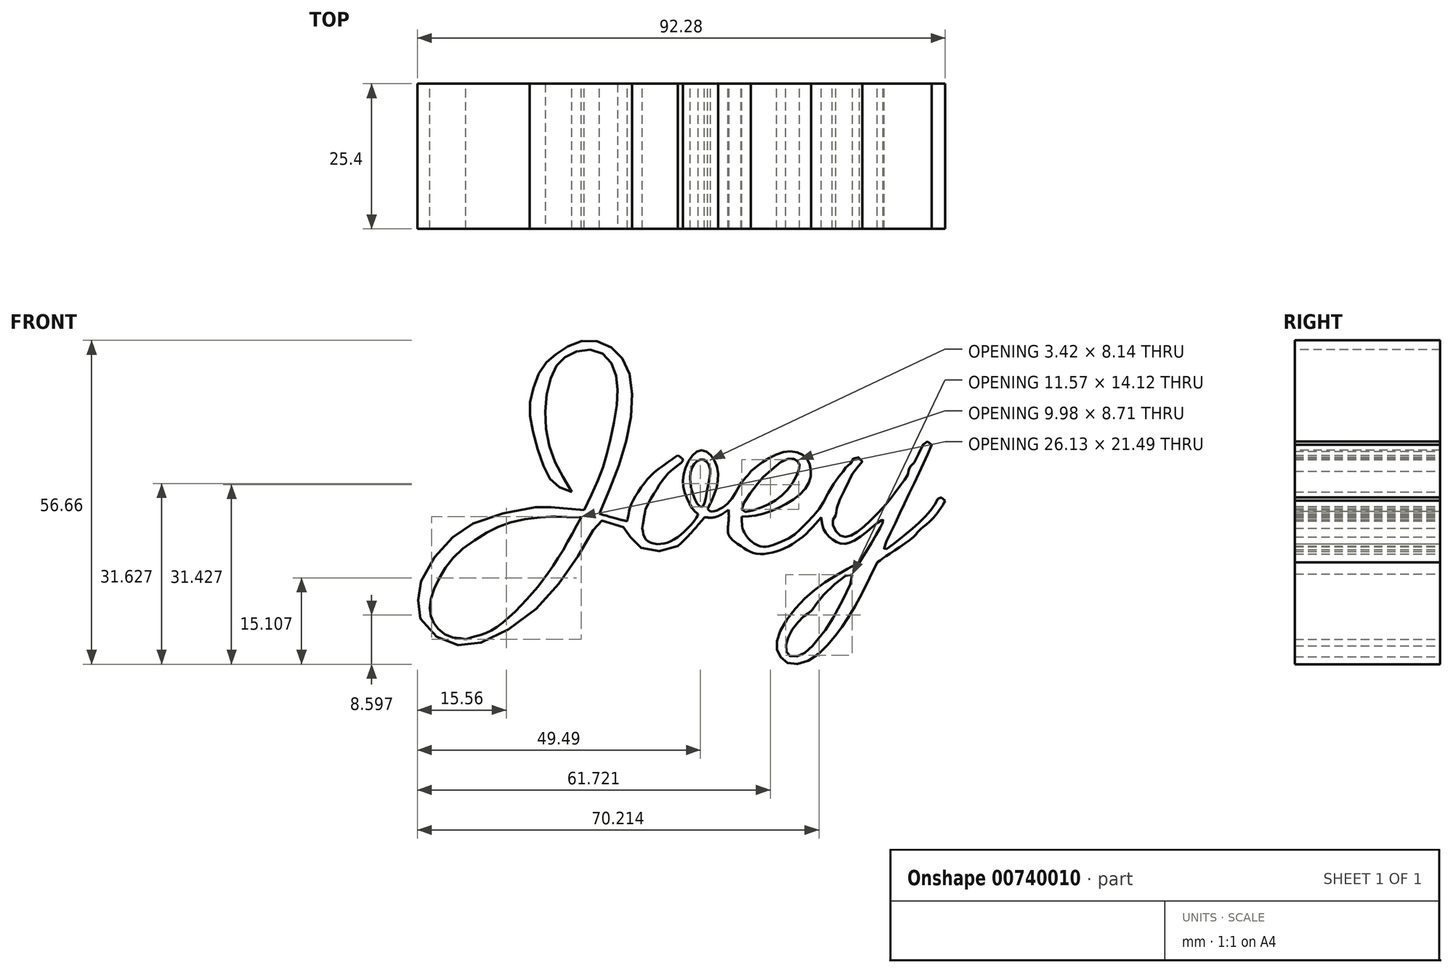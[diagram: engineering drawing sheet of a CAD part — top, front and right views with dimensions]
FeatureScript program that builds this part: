
annotation { "Feature Type Name" : "Feature", "Feature Type Description" : "" }
export const myFeature = defineFeature(function(context is Context, id is Id, definition is map)
    precondition{}
    {
        {
            var Q0;
            Q0=qCreatedBy(makeId("Front.planeOp"),FACE);
            var sketch = newSketch(context, id + "F0", { "sketchPlane" : qUnion([Q0])});
            skFitSpline(sketch, "E0", {"points": [v(-17.96, 22.58) * mm, v(-15.07, 28.97) * mm, v(-13.67, 33.7) * mm, v(-12.17, 41.56) * mm, v(-12.6, 47.01) * mm, v(-15.4, 50.4) * mm, v(-20.27, 49.96) * mm, v(-23.07, 47.3) * mm, v(-24.69, 40.68) * mm, v(-23.66, 32.72) * mm, v(-20.12, 25.8) * mm], "startDerivative": vector(30.1, 62.52) * mm, "endDerivative": vector(35.55, -58.87) * mm});
            skFitSpline(sketch, "E1", {"points": [v(-20.12, 25.8) * mm, v(-23.36, 27.42) * mm, v(-25.57, 31.84) * mm, v(-27.34, 38.61) * mm, v(-27.2, 42.6) * mm, v(-25.28, 47.45) * mm, v(-22.77, 49.96) * mm, v(-18.5, 52.17) * mm, v(-13.5, 51.28) * mm, v(-10.1, 46.72) * mm, v(-10.25, 35.96) * mm, v(-15.26, 21.97) * mm], "startDerivative": vector(-50.27, 16.62) * mm, "endDerivative": vector(-41.8, -97.9) * mm});
            skFitSpline(sketch, "E2", {"points": [v(-15.26, 21.97) * mm, v(-11.6, 20.94) * mm, v(-10.4, 20.67) * mm], "startDerivative": vector(6.52, -1.9) * mm, "endDerivative": vector(2.88, -0.56) * mm});
            skFitSpline(sketch, "E3", {"points": [v(-10.4, 20.67) * mm, v(-10.07, 22.34) * mm, v(-9.83, 23.37) * mm, v(-7.01, 27.85) * mm, v(-4.2, 30.34) * mm, v(-1.58, 32.18) * mm], "startDerivative": vector(2.54, 11.82) * mm, "endDerivative": vector(12.38, 8.58) * mm});
            skFitSpline(sketch, "E4", {"points": [v(-1.58, 32.18) * mm, v(-0.66, 31.3) * mm, v(-2.41, 29.77) * mm, v(-5, 26.66) * mm, v(-7.1, 22.98) * mm, v(-7.36, 21.97) * mm, v(-7.76, 19.44) * mm], "startDerivative": vector(11.74, -6.98) * mm, "endDerivative": vector(-2.67, -16.96) * mm});
            skFitSpline(sketch, "E5", {"points": [v(-17.96, 22.58) * mm, v(-24.78, 23.2) * mm, v(-25.98, 23.2) * mm, v(-33.9, 21.58) * mm, v(-39.38, 19.06) * mm, v(-42.92, 15.84) * mm, v(-46.3, 10.63) * mm, v(-46.88, 7.45) * mm, v(-47.07, 5.45) * mm, v(-45.4, 1.85) * mm, v(-41.55, -0.63) * mm, v(-38.02, -1.06) * mm, v(-32.57, 0.92) * mm, v(-25.2, 6.37) * mm, v(-20, 13.13) * mm, v(-16.25, 19.38) * mm, v(-15.66, 20.85) * mm, v(-12.16, 19.82) * mm, v(-10.4, 19.36) * mm, v(-9.83, 17.94) * mm, v(-8.98, 16.83) * mm, v(-7.1, 15.56) * mm, v(-4.18, 15.53) * mm, v(-1.58, 16.3) * mm], "startDerivative": vector(-148.87, 13.53) * mm, "endDerivative": vector(69.66, 24.55) * mm});
            skFitSpline(sketch, "E6", {"points": [v(-18.46, 21.37) * mm, v(-23.55, 12.53) * mm, v(-29, 5.9) * mm, v(-34.38, 1.4) * mm, v(-37.24, 0.48) * mm, v(-38.64, 0) * mm], "startDerivative": vector(-18, -33.91) * mm, "endDerivative": vector(-12.44, -4.8) * mm});
            skFitSpline(sketch, "E7", {"points": [v(-38.64, 0) * mm, v(-39.6, 0.17) * mm, v(-41.55, 0.52) * mm, v(-43.46, 1.84) * mm, v(-44.34, 3.15) * mm, v(-44.9, 4.99) * mm, v(-44.6, 7.49) * mm, v(-42.93, 11.3) * mm, v(-39.9, 15.18) * mm, v(-34.6, 18.84) * mm, v(-29.64, 20.76) * mm, v(-23.73, 21.49) * mm, v(-23, 21.49) * mm, v(-18.46, 21.37) * mm], "startDerivative": vector(-20.04, 4.15) * mm, "endDerivative": vector(60.78, -1.5) * mm});
            skFitSpline(sketch, "E8", {"points": [v(-7.76, 19.44) * mm, v(-7.04, 17.4) * mm, v(-4.75, 16.66) * mm, v(-1.83, 17.7) * mm, v(1.34, 20.78) * mm, v(2.02, 21.92) * mm], "startDerivative": vector(1.9, -12.67) * mm, "endDerivative": vector(3.32, 6.96) * mm});
            skFitSpline(sketch, "E9", {"points": [v(2.02, 21.92) * mm, v(1.03, 22.84) * mm, v(0, 24.79) * mm, v(-0.66, 27.42) * mm, v(0, 30.41) * mm, v(1.86, 32.91) * mm, v(3.64, 32.7) * mm, v(5.25, 30.26) * mm, v(5.3, 26.87) * mm, v(3.69, 22.84) * mm], "startDerivative": vector(-13.04, 10.03) * mm, "endDerivative": vector(-13.9, -28.86) * mm});
            skFitSpline(sketch, "E10", {"points": [v(3.69, 22.84) * mm, v(4.2, 22.4) * mm, v(5.88, 22.84) * mm, v(7.9, 24.63) * mm, v(9.31, 27.03) * mm, v(10.1, 28.03) * mm, v(11.24, 29.42) * mm], "startDerivative": vector(3.95, -5.47) * mm, "endDerivative": vector(7.15, 8.9) * mm});
            skFitSpline(sketch, "E11", {"points": [v(2.75, 23.2) * mm, v(3.69, 26.66) * mm, v(4.1, 29.84) * mm, v(3.17, 31.3) * mm, v(2.02, 31.3) * mm, v(0.82, 29.79) * mm, v(0.77, 26.56) * mm, v(1.86, 23.75) * mm, v(2.75, 23.2) * mm]});
            skFitSpline(sketch, "E12", {"points": [v(-1.58, 16.3) * mm, v(0.46, 18.29) * mm, v(3.12, 21.37) * mm], "startDerivative": vector(4.38, 4.07) * mm, "endDerivative": vector(4.99, 6) * mm});
            skFitSpline(sketch, "E13", {"points": [v(3.12, 21.37) * mm, v(4.94, 21.37) * mm, v(7.33, 22.65) * mm], "startDerivative": vector(3.98, -0.52) * mm, "endDerivative": vector(4.45, 2.96) * mm});
            skFitSpline(sketch, "E14", {"points": [v(7.33, 22.65) * mm, v(7.33, 20.78) * mm, v(7.33, 18.29) * mm, v(9.52, 16.3) * mm], "startDerivative": vector(0.35, -6.02) * mm, "endDerivative": vector(7.59, -4.77) * mm});
            skFitSpline(sketch, "E15", {"points": [v(9.52, 16.3) * mm, v(12.1, 14.98) * mm, v(16.06, 15.53) * mm, v(20.15, 17.83) * mm, v(23.56, 21.37) * mm], "startDerivative": vector(11.3, -8.06) * mm, "endDerivative": vector(11.8, 13.78) * mm});
            skFitSpline(sketch, "E16", {"points": [v(23.56, 21.37) * mm, v(24.05, 19.06) * mm, v(26.4, 16.9) * mm, v(29.63, 17.46) * mm, v(34.27, 20.92) * mm, v(30.19, 13.5) * mm], "startDerivative": vector(0.97, -15.72) * mm, "endDerivative": vector(-25, -39.63) * mm});
            skFitSpline(sketch, "E17", {"points": [v(30.19, 13.5) * mm, v(24.49, 10.15) * mm, v(19.66, 6.12) * mm, v(16, 0.6) * mm, v(15.94, -2.19) * mm, v(17.81, -4.22) * mm, v(22.2, -3.23) * mm, v(26.04, 0.73) * mm, v(28.9, 4.9) * mm, v(33.34, 13.5) * mm], "startDerivative": vector(-47.56, -26.4) * mm, "endDerivative": vector(30.9, 63.42) * mm});
            skFitSpline(sketch, "E18", {"points": [v(33.34, 13.5) * mm, v(35.47, 14.95) * mm, v(39.95, 18.18) * mm, v(40.63, 19.06) * mm, v(42.24, 20.37) * mm, v(44.6, 23.19) * mm, v(45.19, 24.27) * mm], "startDerivative": vector(10.3, 7.2) * mm, "endDerivative": vector(3.74, 8) * mm});
            skFitSpline(sketch, "E19", {"points": [v(45.19, 24.27) * mm, v(44.3, 24.83) * mm, v(43.58, 23.96) * mm, v(41.81, 21.58) * mm, v(39.09, 19.06) * mm, v(36.52, 16.93) * mm, v(34.56, 15.73) * mm, v(35.47, 18.27) * mm, v(37.9, 23.35) * mm, v(40.63, 29.1) * mm, v(42.87, 34.01) * mm], "startDerivative": vector(-16.85, 15.53) * mm, "endDerivative": vector(16.64, 37.02) * mm});
            skFitSpline(sketch, "E20", {"points": [v(42.87, 34.01) * mm, v(41.72, 34.54) * mm, v(39.74, 30.84) * mm, v(38.91, 30) * mm, v(38.7, 28.96) * mm, v(37.6, 27.24) * mm, v(35.37, 24.27) * mm, v(32.3, 20.92) * mm, v(29.48, 18.6) * mm, v(27.6, 17.92) * mm, v(26.4, 18.54) * mm, v(25.47, 20.37) * mm, v(26.04, 21.72) * mm], "startDerivative": vector(-18.46, 17.74) * mm, "endDerivative": vector(13.08, 18.61) * mm});
            skFitSpline(sketch, "E21", {"points": [v(26.04, 21.72) * mm, v(26.57, 23.96) * mm, v(28.28, 27.5) * mm, v(29.38, 29.59) * mm, v(30.68, 31.3) * mm, v(29.48, 31.88) * mm, v(28.9, 31.05) * mm, v(27.87, 30.1) * mm, v(27.3, 29.27) * mm, v(26.04, 27.71) * mm, v(24.05, 24.27) * mm, v(22.66, 22.14) * mm, v(20.21, 19.59) * mm, v(18.6, 18.13) * mm, v(16.56, 17.09) * mm], "startDerivative": vector(4, 28.51) * mm, "endDerivative": vector(-29.7, -13.17) * mm});
            skFitSpline(sketch, "E22", {"points": [v(16.56, 17.09) * mm, v(13.58, 16.18) * mm, v(11.4, 17.09) * mm, v(9.9, 19.06) * mm, v(9.64, 20.92) * mm], "startDerivative": vector(-10.9, -4.84) * mm, "endDerivative": vector(-0.2, 8.46) * mm});
            skFitSpline(sketch, "E23", {"points": [v(9.64, 20.92) * mm, v(9.64, 21.47) * mm], "startDerivative": vector(0, 0.54) * mm, "endDerivative": vector(0, 0.54) * mm});
            skFitSpline(sketch, "E24", {"points": [v(9.64, 21.47) * mm, v(12.4, 21.7) * mm, v(15.88, 22.92) * mm, v(19.38, 25) * mm, v(21.4, 27.5) * mm, v(21.72, 29.59) * mm, v(21.1, 31.51) * mm, v(19.43, 32.66) * mm, v(16.77, 32.71) * mm, v(13.7, 31.25) * mm, v(11.24, 29.42) * mm], "startDerivative": vector(27.38, 0.62) * mm, "endDerivative": vector(-22.65, -18) * mm});
            skFitSpline(sketch, "E25", {"points": [v(9.64, 22.71) * mm, v(13.54, 28.55) * mm, v(14.06, 28.96) * mm, v(17.45, 31.51) * mm, v(19.48, 31.1) * mm, v(19.53, 29.42) * mm, v(17.03, 25.52) * mm, v(12.7, 22.92) * mm, v(9.64, 22.71) * mm]});
            skFitSpline(sketch, "E26", {"points": [v(28.9, 11.3) * mm, v(24.11, 1.4) * mm, v(23.37, 0.6) * mm, v(20.87, -2.2) * mm, v(18.07, -2.94) * mm, v(17.33, -1.47) * mm, v(18.3, 1.4) * mm, v(20.57, 4.13) * mm, v(21.68, 4.9) * mm, v(23.52, 7.3) * mm, v(28.9, 11.3) * mm]});
            skSolve(sketch);
        }
        {
            var Q0;
            Q0 = qSketchRegion(id + "F0", true);
            extrude(context, id + "F1", {"entities" : qUnion([Q0]), "depth" : 25.4 * mm, "offsetDistance" : 25.4 * mm});
        }
    });
